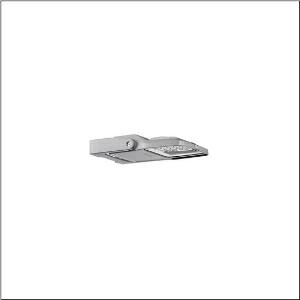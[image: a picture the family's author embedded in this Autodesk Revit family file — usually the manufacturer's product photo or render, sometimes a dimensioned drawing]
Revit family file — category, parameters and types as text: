
# Revit family: floodlight_fl_21_iq_micro___pl61_5xa7762a2c2a_d8df
name_source: partatom
category: Lighting Fixtures
units: mm (PartAtom-declared; Revit-internal decimal feet)

## family parameters
Cut with Voids When Loaded = No
Host = Face
Light Source = No
Part Type = Normal
Room Calculation Point = No
Round Connector Dimension = Use Diameter
Shared = No

## types (1)
- --- (1 x LED, 2910 lm, 23.1 W, 3000K)
    Apparent Load = 23 VA
    CIE Flux Codes = 33 65 98 100 100
    Color Rendering = 70
    Color Temperature = 3000K
    Default Elevation = 1800 mm
    Description = Floodlight FL 21 iQ micro, floodlight, primary light control with lens, of PMMA, primary optical cover: protective disc, of toughened safety glass, transparent, light distribution: PL61, light emission: direct distribution, installation type: surface-mounted, LED, High Power LED, rated luminous flux: 2.910lm, luminous efficacy: 126lm/W, light colour: 730, colour temperature: 3000K, control: Auto-Match, Temp-Guard, Night-Set, Smart-Wire, Desk-Remote (wireless, voltage-free reading and setting of iQ features in the workshop via application-optimized NFC function/RFID function), optimised constant luminous flux control (CLO 2.0), Street-Remote, with terminal, 6-pole, mains connection: 220..240V, AC, 50/60Hz, start of lifetime: 23W, end of service life: 24W, reduction: 11W, luminaire housing, of diecast aluminium, powder-coated, Siteco® metallic grey (DB 702S), corrosivity category C5 mid according to DIN EN ISO 12944, sealing non-destructively replaceable, design bracket, of diecast aluminium, powder-coated, Siteco® metallic grey (DB 702S), protection rating (complete): IP66, insulation class (complete): insulation class II (safety insulation), certification: CE, ENEC, VDE, protection symbol: D, impact resistance: IK07, permissible operating ambient temperature: -40..+40°C, permissible operating ambient temperature for outdoor applications: -40..+50°C, standard: DIN EN 12944, LABS conformity tested according to VDMA 24364:2018-05, packaging unit: 1 piece

Light Distribution: PL61
    Height = 65 mm
    Lamp = 1 x LED
    Lamp Light Flux = 2910 lm
    Lamp Power = 23.1 W
    Lamp count = 1
    Length = 312 mm
    Luminous efficacy = 126 lm/W
    Manufacturer = Siteco
    ModVariant = No
    Model = 5XA7762A2C2A
    Mounting Place = Wall
    Mounting Type = Surface mounted
    Number of Poles = 1
    OnlyDefault = Yes
    Power Factor = 1
    Product Name = Floodlight FL 21 iQ micro | PL61
    Product group = floodlight | wall mounted
    ProductGroupID = 2001
    Protection Class = Protection class II
    Protection Degree = IP 66
    RLX_Detail_Level = 1
    RLX_Emergency_Light_Flux = 0 lm
    RLX_Emergency_Type = 0
    RLX_Emergency_Type_DB = No
    RlxData = <blob elided: 97485 chars, md5=0bb1f29f>
    Socket = socket
    Standby Power = 0 W
    System Light Flux = 2910 lm
    System Power = 23 W
    Type Comments = factory setting: luminous flux: 100 % | dim-lin: 254 | 455 mA
    Type Image = l_1006878.jpg
    URL = http://relux.com
    VarID = @adj_147049
    Voltage = 0 V
    Weight = 0.00 kg
    Width = 230 mm

## geometry (parser evidence)
native form markers: Blend x4, Sweep x12
no freeform markers — native parametric forms only
